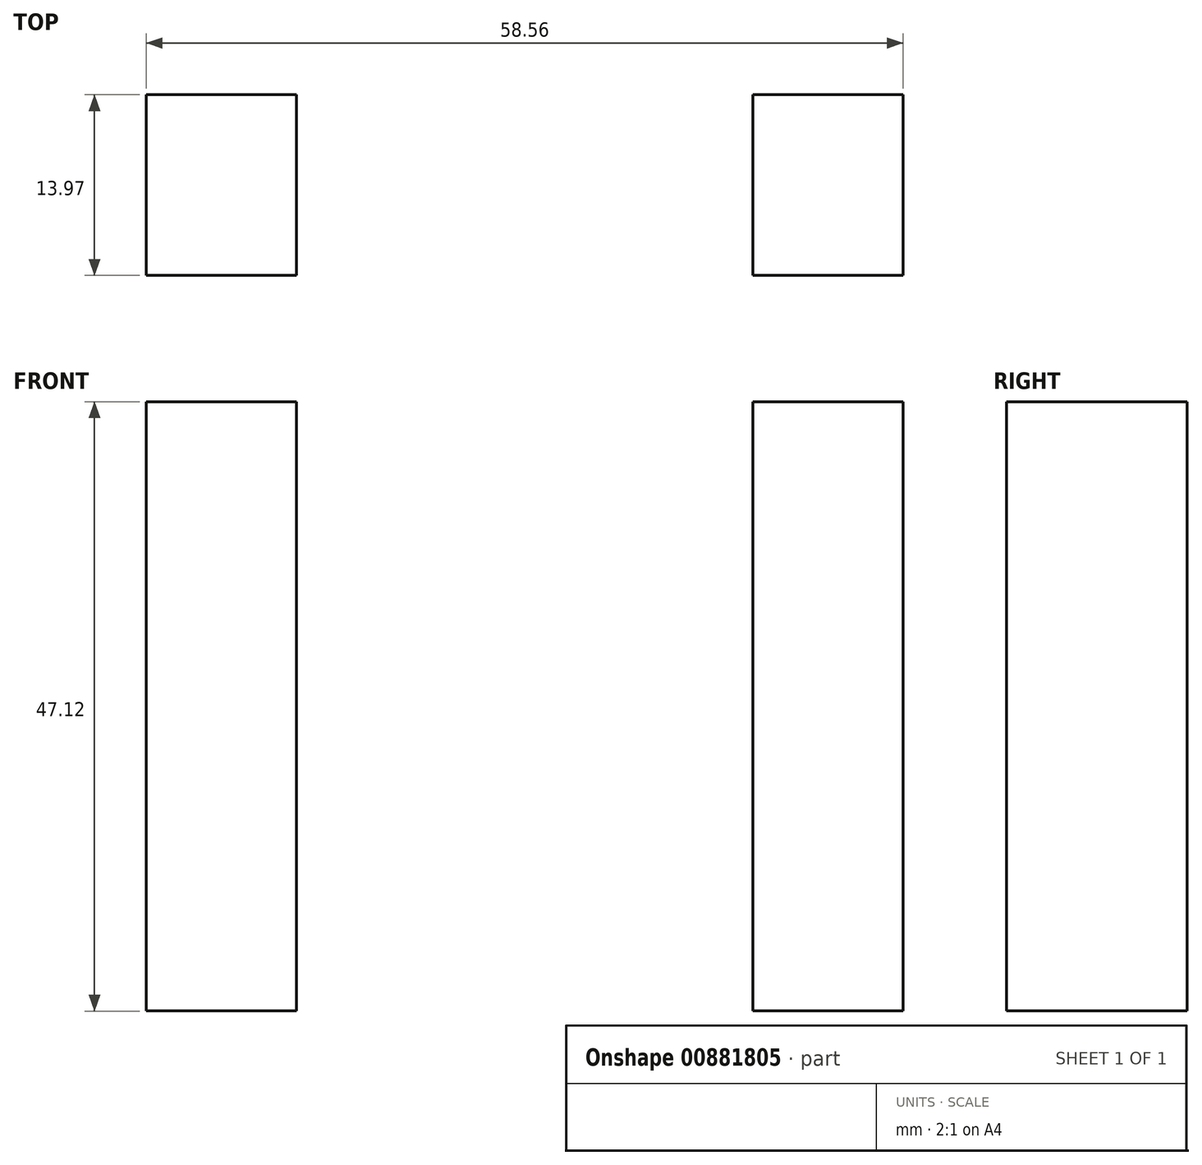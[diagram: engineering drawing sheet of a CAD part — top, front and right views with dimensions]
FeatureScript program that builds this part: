
annotation { "Feature Type Name" : "Feature", "Feature Type Description" : "" }
export const myFeature = defineFeature(function(context is Context, id is Id, definition is map)
    precondition{}
    {
        {
            var Q0;
            Q0=qCreatedBy(makeId("Front.planeOp"),FACE);
            var sketch = newSketch(context, id + "F0", { "sketchPlane" : qUnion([Q0])});
            skLineSegment(sketch, "E0", {"start": v(-17.65, 25.53) * mm, "end": v(-29.28, 25.53) * mm});
            skLineSegment(sketch, "E1", {"start": v(-29.28, 25.53) * mm, "end": v(-29.28, -21.59) * mm});
            skLineSegment(sketch, "E2", {"start": v(-29.28, -21.59) * mm, "end": v(-17.65, -21.59) * mm});
            skLineSegment(sketch, "E3", {"start": v(-17.65, 25.53) * mm, "end": v(-17.65, -21.59) * mm});
            skLineSegment(sketch, "E4.MirrorCS", {"start": v(17.65, 25.53) * mm, "end": v(17.65, -21.59) * mm});
            skLineSegment(sketch, "E5.MirrorCS", {"start": v(17.65, 25.53) * mm, "end": v(29.28, 25.53) * mm});
            skLineSegment(sketch, "E6.MirrorCS", {"start": v(29.28, 25.53) * mm, "end": v(29.28, -21.59) * mm});
            skLineSegment(sketch, "E7.MirrorCS", {"start": v(29.28, -21.59) * mm, "end": v(17.65, -21.59) * mm});
            skSolve(sketch);
        }
        {
            var Q0;
            Q0=makeQuery(id+"F0.imprint","IMPRINT",FACE,{"disambiguationData":[TD([[makeQuery(id+"F0.imprint","IMPRINT",EDGE,{"derivedFrom":sQuery(id+"F0.wireOp",EDGE,"E0")}),1.0]])]});
            var Q1;
            Q1=makeQuery(id+"F0.imprint","IMPRINT",FACE,{"disambiguationData":[TD([[makeQuery(id+"F0.imprint","IMPRINT",EDGE,{"derivedFrom":sQuery(id+"F0.wireOp",EDGE,"E4.MirrorCS")}),1.0]])]});
            extrude(context, id + "F1", {"entities" : qUnion([Q0, Q1]), "depth" : 13.97 * mm, "offsetDistance" : 25.4 * mm});
        }
    });
